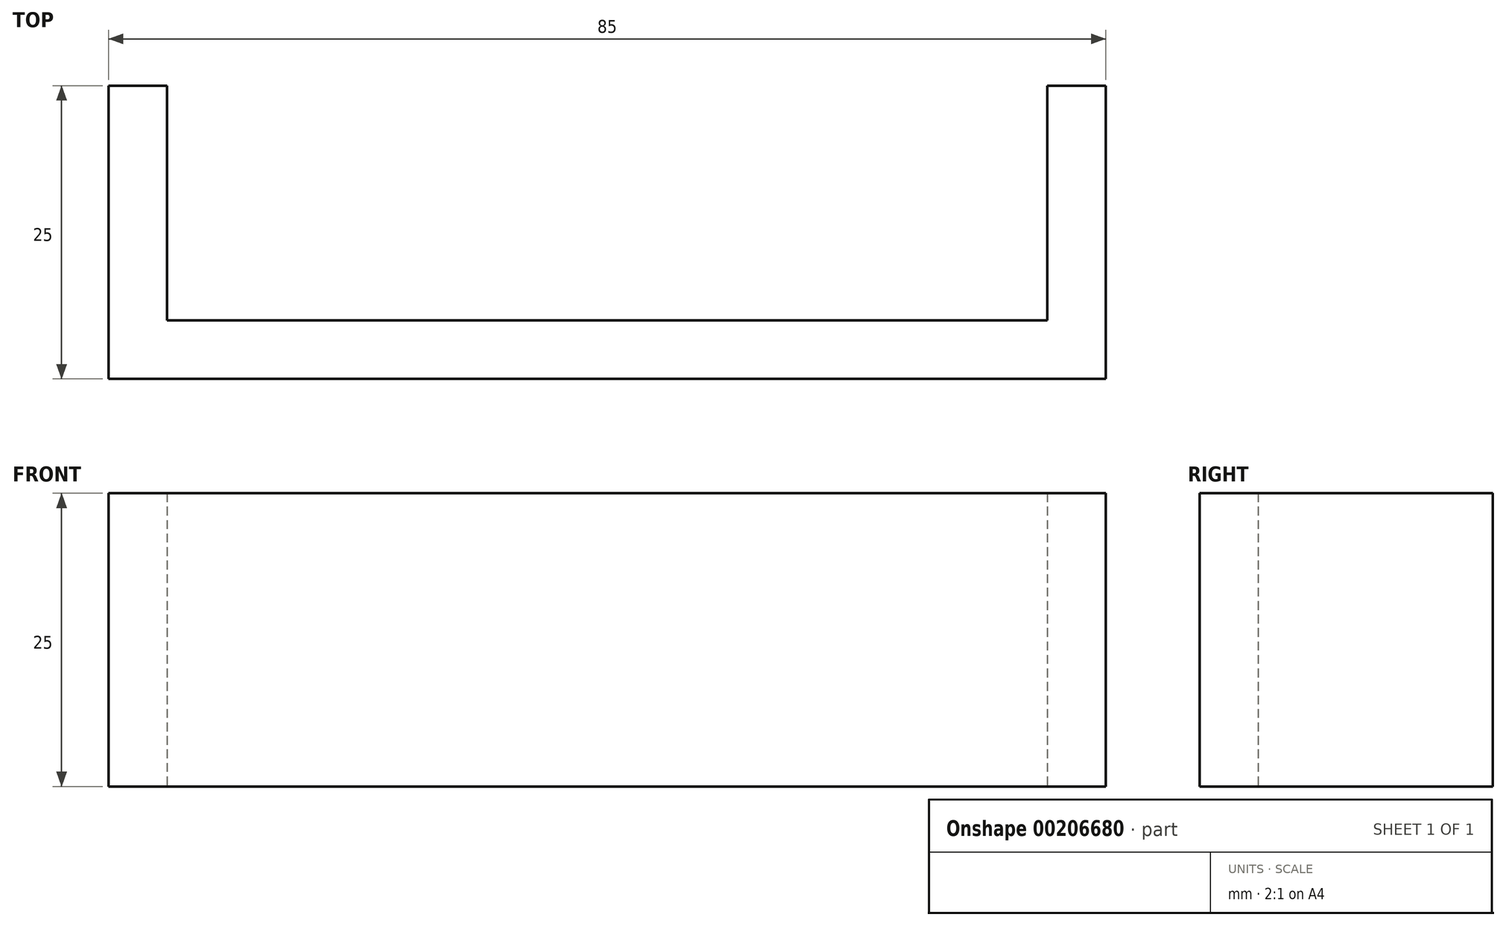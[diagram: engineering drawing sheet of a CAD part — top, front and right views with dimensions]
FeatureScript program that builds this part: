
annotation { "Feature Type Name" : "Feature", "Feature Type Description" : "" }
export const myFeature = defineFeature(function(context is Context, id is Id, definition is map)
    precondition{}
    {
        {
            var Q0;
            Q0=qCreatedBy(makeId("Top.planeOp"),FACE);
            var sketch = newSketch(context, id + "F0", { "sketchPlane" : qUnion([Q0])});
            skLineSegment(sketch, "E0", {"start": v(0, 0) * mm, "end": v(0, 25) * mm});
            skLineSegment(sketch, "E1", {"start": v(0, 25) * mm, "end": v(5, 25) * mm});
            skLineSegment(sketch, "E2", {"start": v(5, 25) * mm, "end": v(5, 5) * mm});
            skLineSegment(sketch, "E3", {"start": v(5, 5) * mm, "end": v(80, 5) * mm});
            skLineSegment(sketch, "E4", {"start": v(80, 5) * mm, "end": v(80, 25) * mm});
            skLineSegment(sketch, "E5", {"start": v(80, 25) * mm, "end": v(85, 25) * mm});
            skLineSegment(sketch, "E6", {"start": v(85, 25) * mm, "end": v(85, 0) * mm});
            skLineSegment(sketch, "E7", {"start": v(85, 0) * mm, "end": v(0, 0) * mm});
            skSolve(sketch);
        }
        {
            var Q0;
            Q0=makeQuery(id+"F0.imprint","IMPRINT",FACE,{"disambiguationData":[TD([[makeQuery(id+"F0.imprint","IMPRINT",EDGE,{"derivedFrom":sQuery(id+"F0.wireOp",EDGE,"E0")}),-1.0]])]});
            extrude(context, id + "F1", {"entities" : qUnion([Q0]), "depth" : 25 * mm});
        }
    });
